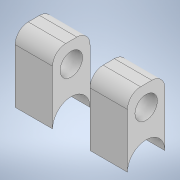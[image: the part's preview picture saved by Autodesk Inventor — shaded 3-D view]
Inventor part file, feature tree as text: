
AUTODESK INVENTOR PART (.ipt)
format: ipt  version: 2021 (Build 250183000, 183)  size: 129,024 bytes
history: native  units: in
note: dims shown in document units (in); Inventor stores cm internally (conversion verified against a paired STEP export)
features: extrude x2, sketch x2
ambient origin geometry x8: Origin, YZ Plane, XZ Plane, XY Plane, X Axis, Y Axis, Z Axis, Center Point
bodies: Solid1 (feature_tree)
feature tree (4):
  extrude  "Extrusion1"  Depth=1.0in
  extrude  "Extrusion2"  Depth=0.5in
  sketch  "Sketch1"  dims[d1=1.0in d2=0.6in]
  sketch  "Sketch2"  dims[d3=0.35in d5=0.5in d6=1.8in d7=1.25in d8=3.0in d9=0.0in d10=1.0in d11=3.0in d12=3.0in d13=0.0in]
